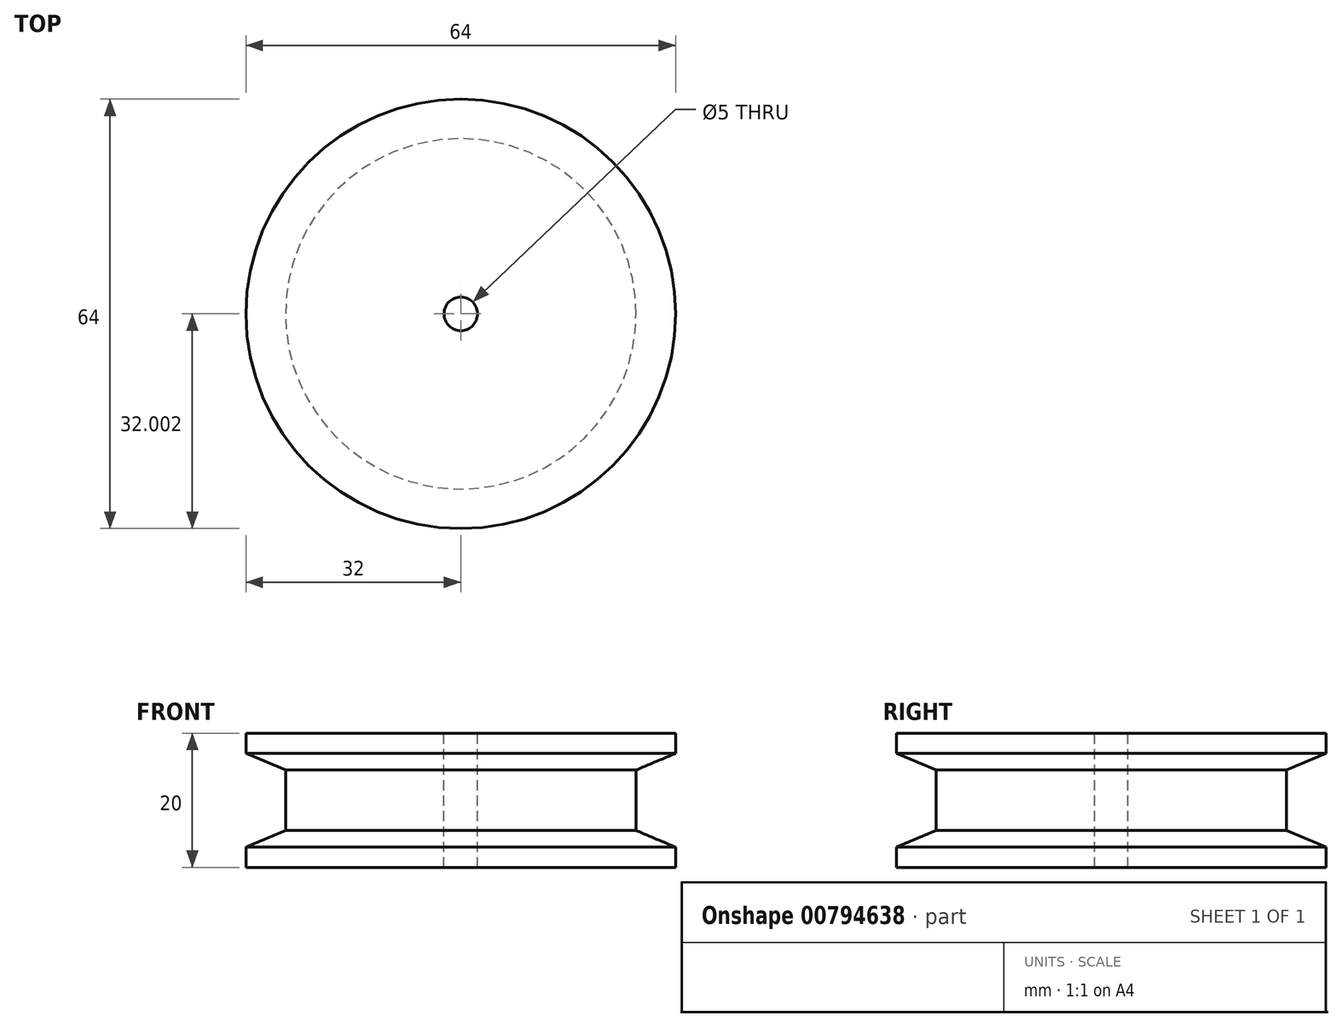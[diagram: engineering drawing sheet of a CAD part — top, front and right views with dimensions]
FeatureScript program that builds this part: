
annotation { "Feature Type Name" : "Feature", "Feature Type Description" : "" }
export const myFeature = defineFeature(function(context is Context, id is Id, definition is map)
    precondition{}
    {
        {
            var Q0;
            Q0=qCreatedBy(makeId("Right.planeOp"),FACE);
            var sketch = newSketch(context, id + "F0", { "sketchPlane" : qUnion([Q0])});
            skLineSegment(sketch, "E0.bottom", {"start": v(-79.73, 0.65) * mm, "end": v(-47.73, 0.65) * mm});
            skLineSegment(sketch, "E0.top", {"start": v(-79.73, -19.35) * mm, "end": v(-47.73, -19.35) * mm});
            skLineSegment(sketch, "E0.right", {"start": v(-47.73, 0.65) * mm, "end": v(-47.73, -19.35) * mm});
            skLineSegment(sketch, "E1", {"start": v(-79.73, 0.65) * mm, "end": v(-79.73, -2.35) * mm});
            skLineSegment(sketch, "E2", {"start": v(-79.73, -2.35) * mm, "end": v(-73.84, -4.85) * mm});
            skLineSegment(sketch, "E3", {"start": v(-73.84, -4.85) * mm, "end": v(-73.84, -13.85) * mm});
            skLineSegment(sketch, "E4", {"start": v(-73.84, -13.85) * mm, "end": v(-79.73, -16.35) * mm});
            skLineSegment(sketch, "E5", {"start": v(-79.73, -16.35) * mm, "end": v(-79.73, -19.35) * mm});
            skLineSegment(sketch, "E6", {"start": v(-42.73, 13.95) * mm, "end": v(-42.73, -30.9) * mm, "construction": true});
            skSolve(sketch);
        }
        {
            var Q0;
            Q0=makeQuery(id+"F0.imprint","IMPRINT",FACE,{"disambiguationData":[TD([[makeQuery(id+"F0.imprint","IMPRINT",EDGE,{"derivedFrom":sQuery(id+"F0.wireOp",EDGE,"E0.bottom")}),-1.0]])]});
            var Q1;
            Q1=sQuery(id+"F0.wireOp",EDGE,"E0.right");
            revolve(context, id + "F1", {"surfaceOperationType" : NewSurfaceOperationType.NEW, "entities" : qUnion([Q0]), "axis" : qUnion([Q1]), "revolveType" : RevolveType.FULL});
        }
        {
            var Q0;
            Q0=makeQuery(id+"F1.opRevolve","SWEPT_FACE",FACE,{"disambiguationData":[OSD([sQuery(id+"F0.wireOp",EDGE,"E0.bottom")])]});
            var sketch = newSketch(context, id + "F2", { "sketchPlane" : qUnion([Q0])});
            skCircle(sketch, "E7", {"center": v(0, -47.73) * mm, "radius": 2.5 * mm});
            skSolve(sketch);
        }
        {
            var Q0;
            Q0=makeQuery(id+"F2.imprint","IMPRINT",FACE,{"disambiguationData":[TD([[makeQuery(id+"F2.imprint","IMPRINT",EDGE,{"derivedFrom":sQuery(id+"F2.wireOp",EDGE,"E7")}),1.0]])]});
            var Q1;
            Q1=makeQuery(id+"F1.opRevolve","SWEPT_FACE",FACE,{"disambiguationData":[OSD([sQuery(id+"F0.wireOp",EDGE,"E0.top")])]});
            extrude(context, id + "F3", {"entities" : qUnion([Q0]), "operationType" : NewBodyOperationType.REMOVE, "endBound" : BoundingType.UP_TO_SURFACE, "oppositeDirection" : true, "depth" : 5 * mm, "endBoundEntityFace" : qUnion([Q1]), "offsetDistance" : 25 * mm});
        }
    });
